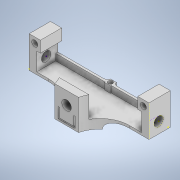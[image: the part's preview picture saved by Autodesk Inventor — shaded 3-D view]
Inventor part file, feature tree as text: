
AUTODESK INVENTOR PART (.ipt)
format: ipt  version: 2020.1 (Build 241239000, 239)  size: 410,112 bytes
history: native  units: mm
features: sketch x38, extrude x22, fillet x6
ambient origin geometry x8: Origin, YZ Plane, XZ Plane, XY Plane, X Axis, Y Axis, Z Axis, Center Point
bodies: Solid1 (feature_tree)
feature tree (66):
  sketch  "Sketch1"  dims[d3=25.4mm d4=25.4mm]
  extrude  "Extrusion1"  Depth=25.4mm
  extrude  "Extrusion2"  Depth=10.0mm TaperAngle=0.0deg
  extrude  "Extrusion3"  Depth=15.0mm
  sketch  "Sketch5"  dims[d14=14.85mm d15=0.0mm d18=2.0mm]
  sketch  "Sketch6"  dims[d19=3.25mm d20=150.0mm d21=10.0mm d22=0.0mm d23=0.0mm]
  extrude  "Extrusion4"  Depth=25.4mm TaperAngle=0.0deg
  sketch  "Sketch8"  dims[d27=15.0mm d28=8.0mm]
  extrude  "Extrusion5"  Depth=2.0mm
  extrude  "Extrusion6"  Depth=10.0mm TaperAngle=0.0deg
  sketch  "Sketch11"  dims[d35=14.9mm d36=0.0mm d37=14.9mm d38=0.0mm]
  extrude  "Extrusion7"  Depth=10.0mm
  extrude  "Extrusion8"  Depth=8.0mm
  extrude  "Extrusion9"  Depth=18.0mm
  sketch  "Sketch14"  dims[d45=31.75mm d46=10.0mm d47=0.0mm]
  extrude  "Extrusion10"  Depth=7.4mm
  extrude  "Extrusion11"  Depth=14.9mm TaperAngle=0.0deg
  sketch  "Sketch19"  dims[d60=1.5875mm d61=6.35mm d63=8.0mm d64=20.0mm d65=0.0mm d66=15.0mm d67=0.0mm]
  sketch  "Sketch20"  dims[d68=9.0mm d71=3.0mm d72=0.0mm]
  extrude  "Extrusion12"  Depth=20.0mm TaperAngle=0.0deg
  extrude  "Extrusion13"  Depth=10.0mm TaperAngle=0.0deg
  sketch  "Sketch23"  dims[d79=1.0mm d80=3.0mm d81=0.0mm]
  extrude  "Extrusion14"  Depth=10.0mm TaperAngle=0.0deg
  extrude  "Extrusion15"  Depth=10.0mm TaperAngle=0.0deg
  fillet  "Fillet1"  Radius=21.0mm
  sketch  "Sketch26"  dims[d85=11.75mm d86=0.0mm]
  sketch  "Sketch27"  dims[d87=12.0mm d88=0.0mm]
  sketch  "Sketch28"  dims[d89=5.0mm]
  sketch  "Sketch29"  dims[d90=0.502mm d91=0.0mm]
  extrude  "Extrusion16"  Depth=1.5875mm
  sketch  "Sketch31"  dims[d94=39.25mm]
  sketch  "Sketch32"
  extrude  "Extrusion17"  Depth=6.35mm
  fillet  "Fillet2"  Radius=8.0mm
  fillet  "Fillet3"  Radius=20.0mm
  fillet  "Fillet4"  Radius=15.0mm
  sketch  "Sketch34"
  extrude  "Extrusion18"  Depth=3.0mm TaperAngle=0.0deg
  sketch  "Sketch36"
  extrude  "Extrusion19"  Depth=2.5mm
  extrude  "Extrusion20"  Depth=0.5mm
  fillet  "Fillet5"  Radius=1.0mm
  extrude  "Extrusion21"  Depth=3.0mm TaperAngle=0.0deg
  extrude  "Extrusion22"  Depth=8.0mm
  fillet  "Fillet6"  Radius=8.0mm
  sketch  "Sketch41"
  sketch  "Sketch2"  dims[d5=12.7mm d6=10.0mm d7=0.0mm]
  sketch  "Sketch3"  dims[d8=15.0mm d9=15.0mm]
  sketch  "Sketch4"  dims[d10=8.0mm d11=25.4mm d12=0.0mm]
  sketch  "Sketch7"  dims[d24=10.0mm d25=0.0mm d26=15.0mm]
  sketch  "Sketch9"  dims[d29=25.4mm d30=0.0mm d31=18.0mm]
  sketch  "Sketch10"  dims[d32=25.4mm d33=0.0mm d34=7.4mm]
  sketch  "Sketch12"  dims[d39=31.75mm d40=20.0mm d41=0.0mm]
  sketch  "Sketch13"  dims[d42=25.0mm d43=10.0mm d44=0.0mm]
  sketch  "Sketch17"  dims[d48=12.7mm d49=10.0mm d50=0.0mm d51=21.0mm]
  sketch  "Sketch18"  dims[d58=1.5875mm d59=1.5875mm]
  sketch  "Sketch21"  dims[d73=2.5mm d74=2.5mm]
  sketch  "Sketch22"  dims[d75=3.0mm d76=0.0mm d77=0.5mm d78=1.0mm]
  sketch  "Sketch25"  dims[d82=6.25mm d83=8.0mm d84=8.0mm]
  sketch  "Sketch30"  dims[d92=1.0mm d93=0.0mm]
  sketch  "Sketch33"
  sketch  "Sketch35"
  sketch  "Sketch37"
  sketch  "Sketch38"
  sketch  "Sketch39"
  sketch  "Sketch40"
